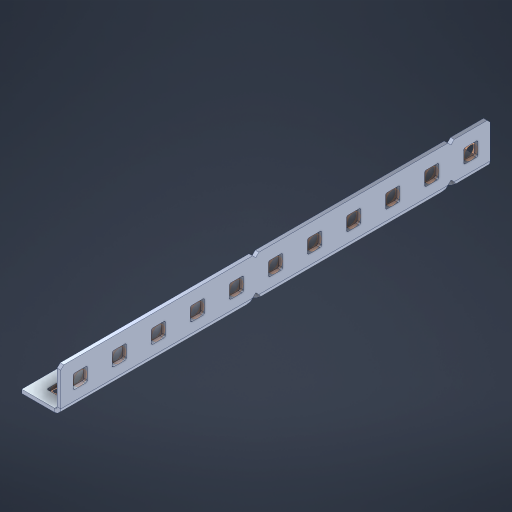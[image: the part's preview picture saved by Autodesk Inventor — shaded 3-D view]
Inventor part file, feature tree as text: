
AUTODESK INVENTOR PART (.ipt)
format: ipt  version: 2023 (Build 270158000, 158)  size: 578,048 bytes
history: native  units: in
note: dims shown in document units (in); Inventor stores cm internally (conversion verified against a paired STEP export)
features: other x27, extrude x21, sheet_metal_op x10, sketch x8, mirror x1, pattern_linear x1, chamfer x1
ambient origin geometry x8: Origin, YZ Plane, XZ Plane, XY Plane, X Axis, Y Axis, Z Axis, Center Point
bodies: Solid1 (feature_tree), Body (feature_tree)
feature tree (69):
  other  "Flange Pattern Plane"
  sheet_metal_op  "Flange Pattern"
  sheet_metal_op  "Body Pattern"
  other  "Arc Length"
  mirror  "Notch Mirror"
  pattern_linear  "Notch Pattern"  Spacing1=0.1875in  [1 undecoded]
  chamfer  "End Chamfer"
  extrude  "Half Cut"  Depth=0.0469in
  sketch  "Sketch1"  dims[d0=2.5in]
  other  "Plate1"
  sketch  "Sketch2"  dims[d1=5.5in]
  other  "Plate2"
  sheet_metal_op  "Bend1"
  sheet_metal_op  "Corner1"
  sketch  "Sketch3"  dims[d2=0.0469in]
  other  "Flange Pattern Sketch"
  sketch  "Sketch7"  dims[d3=0.0469in]
  other  "Srf1"
  other  "Srf2"
  sketch  "Sketch8"  dims[d4=0.0234in]
  sketch  "Sketch9"  dims[d5=0.0938in]
  other  "Srf91"
  sheet_metal_op  "Body Pattern Sketch"
  other  "Srf92"
  sketch  "Sketch13"  dims[d6=0.0469in]
  sketch  "Sketch14"  dims[d7=0.5in d8=90.0deg d9=0.0312in d10=0.1875in d11=0.0469in d12=0.0469in d16=0.182in d17=0.02in d18=0.0469in d19=0.0in d20=0.25in d21=0.25in d46=0.172in d47=1.0in d48=0.0in d49=0.182in d50=0.02in d51=0.25in d52=0.25in d53=0.0469in d54=0.0in d55=0.172in d56=1.0in d57=0.0in d60=4.3307in d62=0.5in d63=0.3937in d65=0.5in d85=0.1227in d86=0.1659in d88=0.04in d89=0.0469in d90=0.0in d91=0.04in d92=0.0491in d95=2.5in d96=0.04in d97=0.25in d98=45.0deg d101=0.0in d102=2.497in d131=0.5in d132=4.3307in d134=0.5in d139=0.5in]
  other  "Srf856"
  other  "Srf1310"
  other  "Srf1311"
  other  "Srf1312"
  other  "Srf1376"
  other  "Srf1377"
  other  "Srf1728"
  other  "Srf1755"
  other  "Srf1878"
  other  "Srf1879"
  other  "Srf1880"
  other  "Srf1881"
  other  "Srf1882"
  other  "Srf1942"
  other  "Srf1943"
  other  "Srf1944"
  other  "Srf1945"
  other  "Srf1946"
  sheet_metal_op  "Flange Stamp"
  sheet_metal_op  "Flange Circle"
  sheet_metal_op  "Body Stamp"
  sheet_metal_op  "Body Circle"
  sheet_metal_op  "Notch"
  extrude  "ExtrusionSrf2"  Depth=0.0469in
  extrude  "ExtrusionSrf92"  Depth=0.5in
  extrude  "ExtrusionSrf856"  Depth=0.02in
  extrude  "ExtrusionSrf1310"  Depth=0.0469in
  extrude  "ExtrusionSrf1311"  TaperAngle=0.0deg  [1 undecoded]
  extrude  "ExtrusionSrf1312"  Depth=0.5in
  extrude  "ExtrusionSrf1376"  Depth=0.5in
  extrude  "ExtrusionSrf1377"  Depth=0.5in
  extrude  "ExtrusionSrf1728"  Depth=0.5in TaperAngle=0.0deg
  extrude  "ExtrusionSrf1755"  Depth=0.5in
  extrude  "ExtrusionSrf1878"  Depth=0.02in
  extrude  "ExtrusionSrf1879"  Depth=0.5in
  extrude  "ExtrusionSrf1880"  Depth=0.5in
  extrude  "ExtrusionSrf1881"  Depth=0.0469in
  extrude  "ExtrusionSrf1882"  TaperAngle=0.0deg  [1 undecoded]
  extrude  "ExtrusionSrf1942"  Depth=0.5in
  extrude  "ExtrusionSrf1943"  Depth=0.5in TaperAngle=0.0deg
  extrude  "ExtrusionSrf1944"  Depth=0.5in
  extrude  "ExtrusionSrf1945"  Depth=0.5in
  extrude  "ExtrusionSrf1946"  Depth=0.5in
note: 3 required parameter values undecoded (feature->parameter linkage not recoverable at this tier; creation-order binding heuristic only, values carry confidence <= 0.55)
